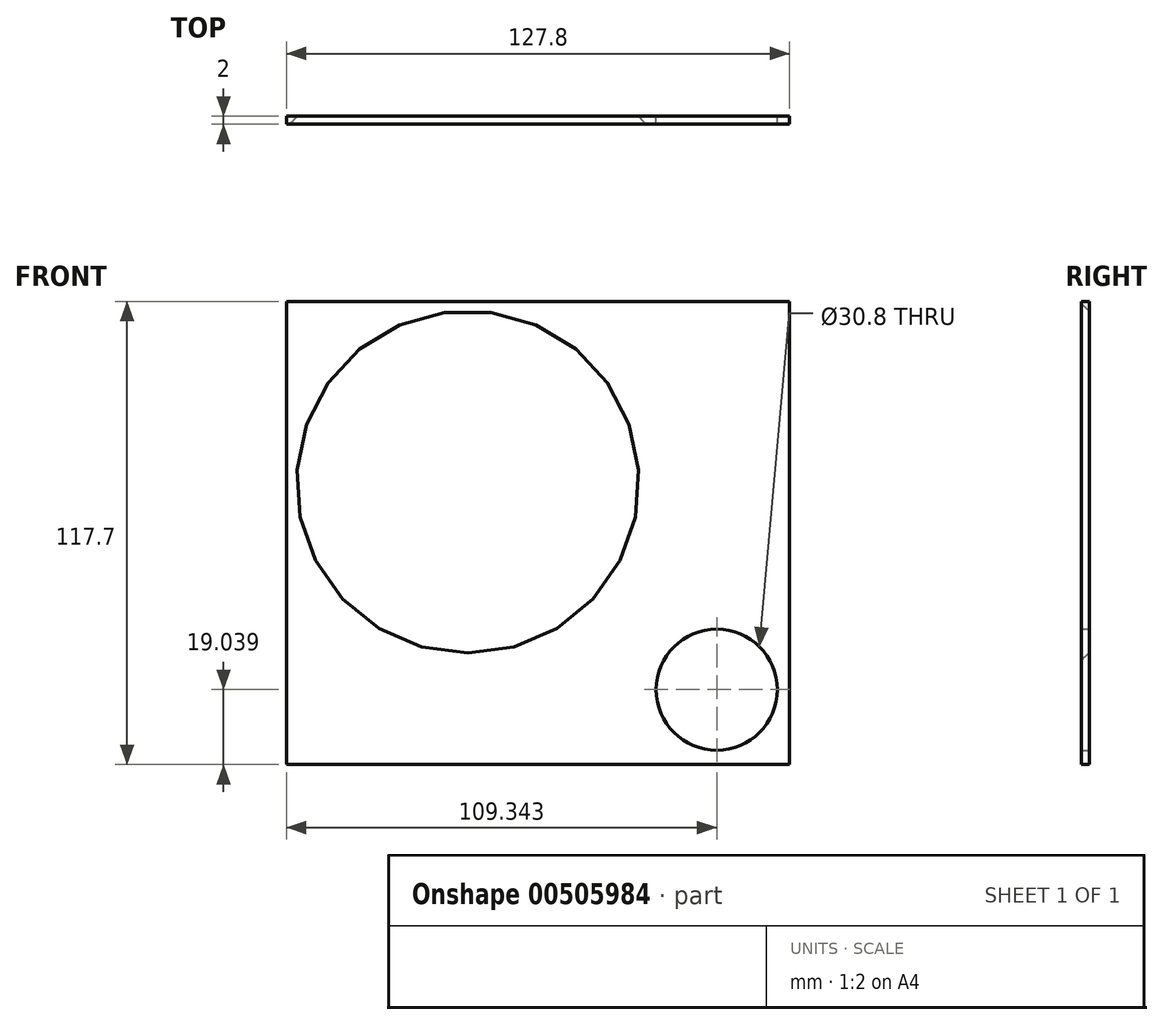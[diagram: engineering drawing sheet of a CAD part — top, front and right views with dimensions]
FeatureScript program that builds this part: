
annotation { "Feature Type Name" : "Feature", "Feature Type Description" : "" }
export const myFeature = defineFeature(function(context is Context, id is Id, definition is map)
    precondition{}
    {
        {
            var Q0;
            Q0=qCreatedBy(makeId("Front.planeOp"),FACE);
            var sketch = newSketch(context, id + "F0", { "sketchPlane" : qUnion([Q0])});
            skLineSegment(sketch, "E0.bottom", {"start": v(63.9, 58.85) * mm, "end": v(-63.9, 58.85) * mm});
            skLineSegment(sketch, "E0.top", {"start": v(63.9, -58.85) * mm, "end": v(-63.9, -58.85) * mm});
            skLineSegment(sketch, "E0.left", {"start": v(63.9, 58.85) * mm, "end": v(63.9, -58.85) * mm});
            skLineSegment(sketch, "E0.right", {"start": v(-63.9, 58.85) * mm, "end": v(-63.9, -58.85) * mm});
            skLineSegment(sketch, "E1", {"start": v(-63.9, 0) * mm, "end": v(-52.75, 0) * mm});
            skLineSegment(sketch, "E2.trimOffspring", {"start": v(-42.75, 0) * mm, "end": v(63.9, 0) * mm});
            skCircle(sketch, "E3", {"center": v(45.44, -39.81) * mm, "radius": 13.4 * mm});
            skCircle(sketch, "E4.0", {"center": v(45.44, -39.81) * mm, "radius": 15.4 * mm});
            skCircle(sketch, "E5", {"center": v(-17.82, 12.97) * mm, "radius": 43.5 * mm});
            skCircle(sketch, "E6", {"center": v(-17.82, 12.97) * mm, "radius": 42 * mm});
            skLineSegment(sketch, "E7.bottom", {"start": v(63.9, -58.85) * mm, "end": v(-28.4, -58.85) * mm});
            skLineSegment(sketch, "E7.left", {"start": v(63.9, -58.85) * mm, "end": v(63.9, -32.73) * mm});
            skLineSegment(sketch, "E8.bottom", {"start": v(-63.9, 58.85) * mm, "end": v(-59.43, 58.85) * mm});
            skLineSegment(sketch, "E8.left", {"start": v(-63.9, 58.85) * mm, "end": v(-63.9, -25.72) * mm});
            skLineSegment(sketch, "E8.right", {"start": v(-59.43, 18.61) * mm, "end": v(-59.43, 7.32) * mm});
            skSolve(sketch);
        }
        {
            var Q0;
            Q0 = qSketchRegion(id + "F0", true);
            extrude(context, id + "F1", {"entities" : qUnion([Q0]), "depth" : 2 * mm, "offsetDistance" : 25 * mm});
        }
        {
            var Q0;
            Q0=makeQuery(id+"F1.opExtrude","CAP_EDGE",EDGE,{"disambiguationData":[OSD([sQuery(id+"F0.wireOp",EDGE,"E5")])],"isStart":false});
            fillet(context, id + "F2", {"entities" : qUnion([Q0]), "radius" : 2 * mm, "tangentPropagation" : true, "rho" : .1, "crossSection" : FilletCrossSection.CONIC, "allowEdgeOverflow" : false});
        }
    });
